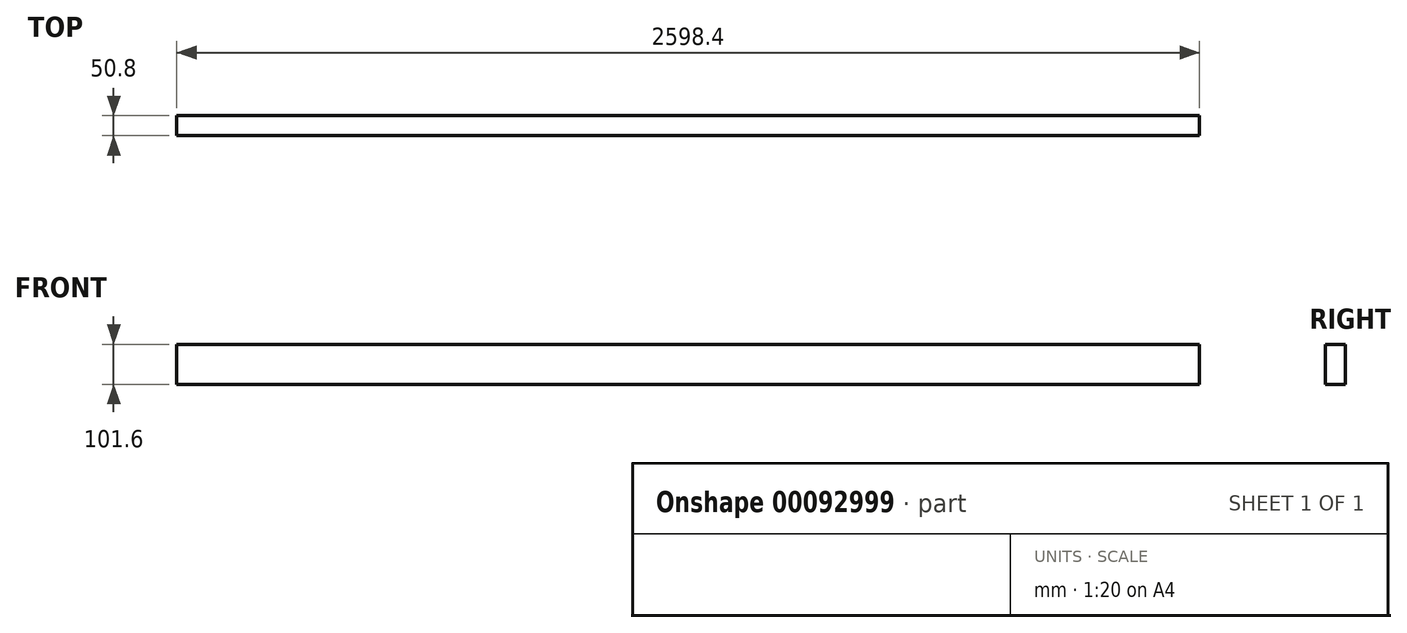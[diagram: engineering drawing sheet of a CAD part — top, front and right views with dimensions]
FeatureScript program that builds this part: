
annotation { "Feature Type Name" : "Feature", "Feature Type Description" : "" }
export const myFeature = defineFeature(function(context is Context, id is Id, definition is map)
    precondition{}
    {
        {
            var Q0;
            Q0=qCreatedBy(makeId("Top.planeOp"),FACE);
            var sketch = newSketch(context, id + "F0", { "sketchPlane" : qUnion([Q0])});
            skLineSegment(sketch, "E0.bottom", {"start": v(-1299.2, 25.4) * mm, "end": v(1299.2, 25.4) * mm});
            skLineSegment(sketch, "E0.top", {"start": v(-1299.2, -25.4) * mm, "end": v(1299.2, -25.4) * mm});
            skLineSegment(sketch, "E1", {"start": v(-1299.2, -25.4) * mm, "end": v(-1299.2, 25.4) * mm});
            skLineSegment(sketch, "E2", {"start": v(1299.2, -25.4) * mm, "end": v(1299.2, 25.4) * mm});
            skSolve(sketch);
        }
        {
            var Q0;
            Q0=qSketchRegion(id+"F0",true);
            extrude(context, id + "F1", {"entities" : qUnion([Q0]), "oppositeDirection" : true, "depth" : 101.6 * mm});
        }
    });
